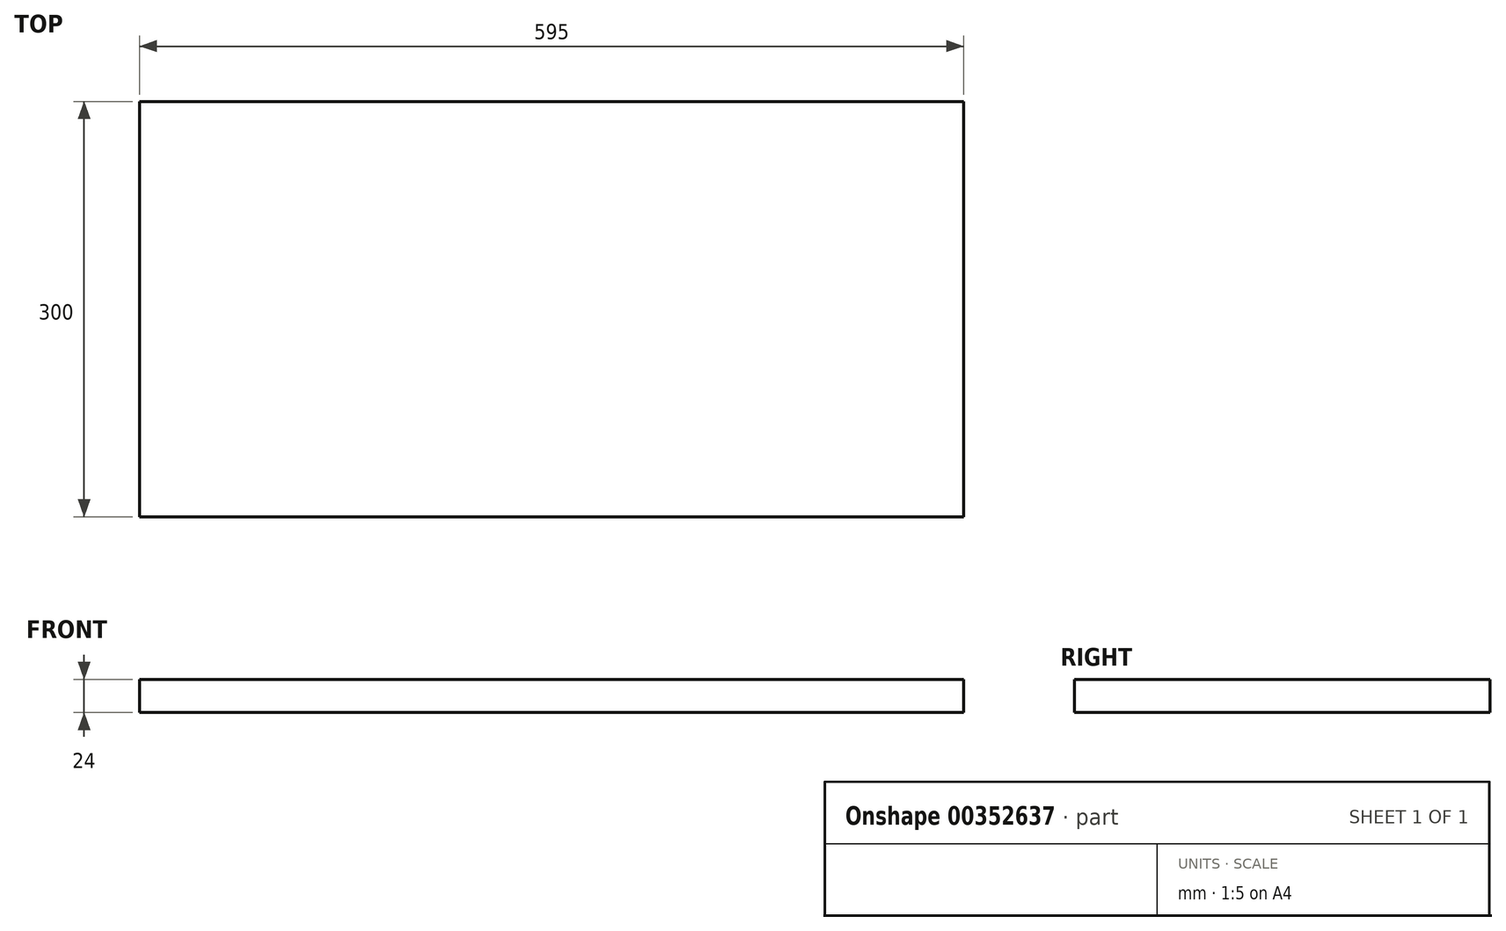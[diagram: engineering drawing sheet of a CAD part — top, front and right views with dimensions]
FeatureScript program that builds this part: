
annotation { "Feature Type Name" : "Feature", "Feature Type Description" : "" }
export const myFeature = defineFeature(function(context is Context, id is Id, definition is map)
    precondition{}
    {
        {
            var Q0;
            Q0=qCreatedBy(makeId("Front.planeOp"),FACE);
            var sketch = newSketch(context, id + "F0", { "sketchPlane" : qUnion([Q0])});
            skLineSegment(sketch, "E0", {"start": v(-58.18, 31.83) * mm, "end": v(-33.18, 31.83) * mm});
            skLineSegment(sketch, "E1", {"start": v(-58.18, 31.83) * mm, "end": v(-346.18, 31.83) * mm});
            skLineSegment(sketch, "E2", {"start": v(-346.18, 31.83) * mm, "end": v(-346.18, 7.83) * mm});
            skLineSegment(sketch, "E3", {"start": v(-346.18, 7.83) * mm, "end": v(-33.18, 7.83) * mm});
            skLineSegment(sketch, "E4", {"start": v(-33.18, 7.83) * mm, "end": v(248.82, 7.83) * mm});
            skLineSegment(sketch, "E5", {"start": v(248.82, 7.83) * mm, "end": v(248.82, 31.83) * mm});
            skLineSegment(sketch, "E6", {"start": v(248.82, 31.83) * mm, "end": v(-33.18, 31.83) * mm});
            skLineSegment(sketch, "E7", {"start": v(-33.18, 31.83) * mm, "end": v(-33.18, 7.83) * mm});
            skLineSegment(sketch, "E8", {"start": v(-58.18, 31.83) * mm, "end": v(-58.18, 7.83) * mm});
            skSolve(sketch);
        }
        {
            var Q0;
            Q0 = qSketchRegion(id + "F0", true);
            extrude(context, id + "F1", {"entities" : qUnion([Q0]), "depth" : 300 * mm});
        }
    });
